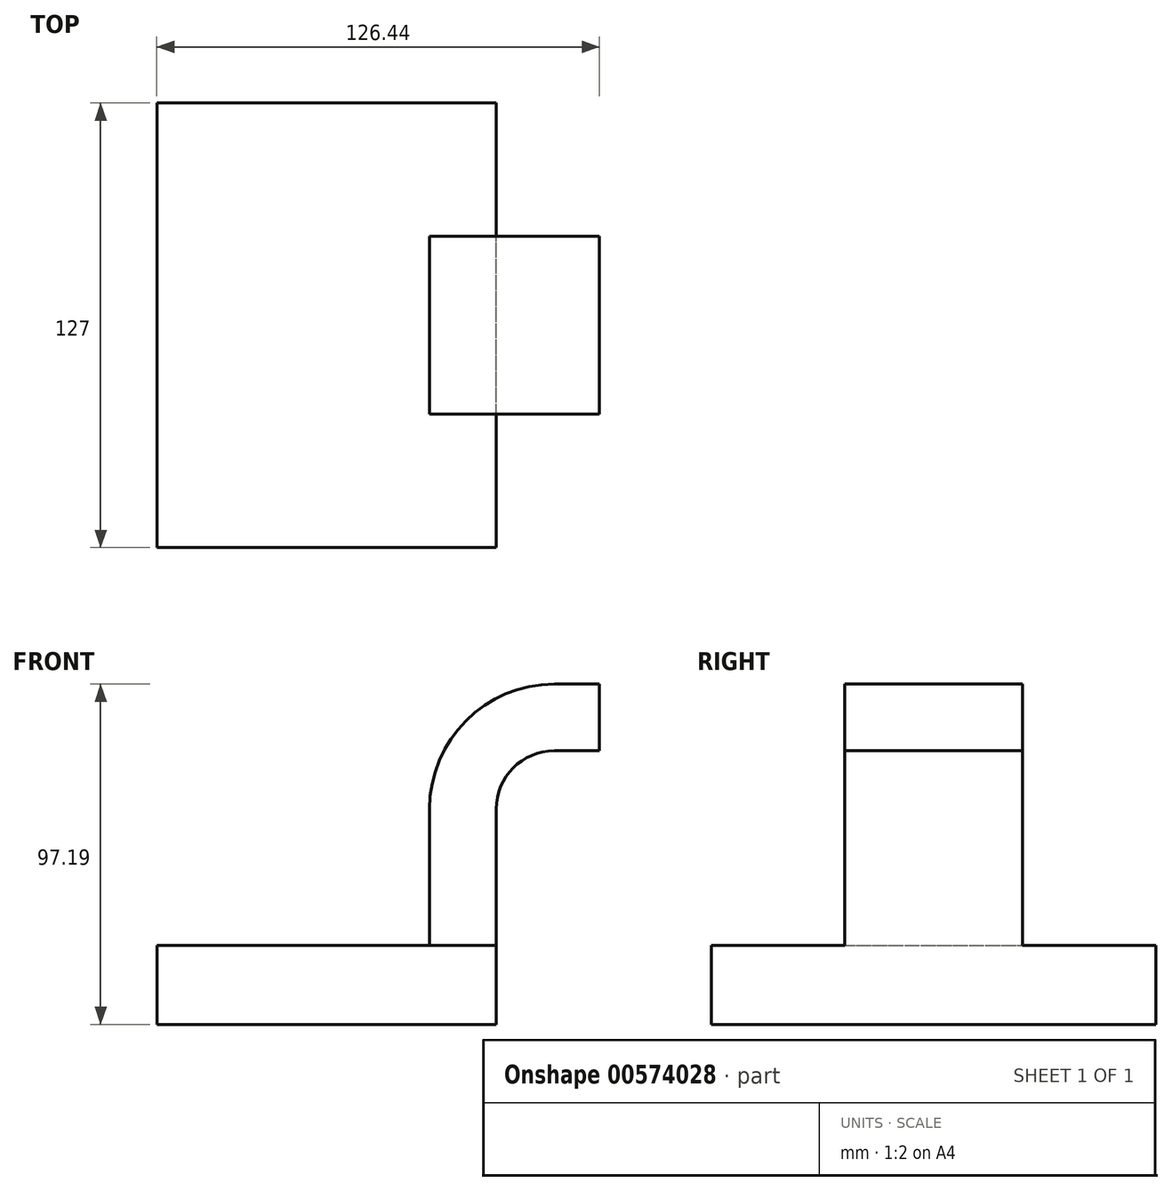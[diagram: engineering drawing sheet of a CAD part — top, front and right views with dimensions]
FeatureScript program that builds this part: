
annotation { "Feature Type Name" : "Feature", "Feature Type Description" : "" }
export const myFeature = defineFeature(function(context is Context, id is Id, definition is map)
    precondition{}
    {
        {
            var Q0;
            Q0=qCreatedBy(makeId("Front.planeOp"),FACE);
            var sketch = newSketch(context, id + "F0", { "sketchPlane" : qUnion([Q0])});
            skLineSegment(sketch, "E0.bottom", {"start": v(48.48, -11.3) * mm, "end": v(-48.48, -11.3) * mm});
            skLineSegment(sketch, "E0.top", {"start": v(48.48, 11.3) * mm, "end": v(-48.48, 11.3) * mm});
            skLineSegment(sketch, "E0.left", {"start": v(48.48, -11.3) * mm, "end": v(48.48, 11.3) * mm});
            skLineSegment(sketch, "E0.right", {"start": v(-48.48, -11.3) * mm, "end": v(-48.48, 11.3) * mm});
            skPoint(sketch, "E0.middle", {"position": v(0, 0) * mm});
            skLineSegment(sketch, "E1.bottom", {"start": v(135.43, 21.72) * mm, "end": v(77.96, 21.72) * mm});
            skLineSegment(sketch, "E1.top", {"start": v(135.43, 90.3) * mm, "end": v(77.96, 90.3) * mm});
            skLineSegment(sketch, "E1.left", {"start": v(135.43, 21.72) * mm, "end": v(135.43, 90.3) * mm});
            skLineSegment(sketch, "E1.right", {"start": v(77.96, 21.72) * mm, "end": v(77.96, 90.3) * mm});
            skPoint(sketch, "E1.middle", {"position": v(106.7, 56) * mm});
            skLineSegment(sketch, "E2", {"start": v(48.48, 11.3) * mm, "end": v(48.48, 50.22) * mm});
            skArc(sketch, "E3", {"start": v(48.48, 50.22) * mm, "mid": v(53.34, 61.97) * mm, "end": v(65.09, 66.84) * mm});
            skLineSegment(sketch, "E4", {"start": v(65.09, 66.84) * mm, "end": v(135.43, 66.84) * mm});
            skLineSegment(sketch, "E5.0", {"start": v(65.09, 85.89) * mm, "end": v(91.95, 85.89) * mm});
            skArc(sketch, "E5.1", {"start": v(29.43, 50.22) * mm, "mid": v(39.87, 75.44) * mm, "end": v(65.09, 85.89) * mm});
            skLineSegment(sketch, "E5.2", {"start": v(29.43, 7.75) * mm, "end": v(29.43, 50.22) * mm});
            skFitSpline(sketch, "E6", {"points": [v(-48.48, 11.3) * mm, v(65.09, 85.89) * mm], "startDerivative": vector(35.98, 132.5) * mm, "endDerivative": vector(154.78, -0.2) * mm});
            skSolve(sketch);
        }
        {
            var Q0;
            Q0=makeQuery(id+"F0.imprint","IMPRINT",FACE,{"disambiguationData":[TD([[makeQuery(id+"F0.imprint","IMPRINT",EDGE,{"derivedFrom":sQuery(id+"F0.wireOp",EDGE,"E0.bottom")}),-1.0]])]});
            extrude(context, id + "F1", {"entities" : qUnion([Q0]), "endBound" : BoundingType.SYMMETRIC, "depth" : 127 * mm, "offsetDistance" : 25.4 * mm});
        }
        {
            var Q0;
            {var subQ1=sQuery(id+"F0.wireOp",EDGE,"E2");Q0=makeQuery(id+"F0.imprint","IMPRINT",FACE,{"disambiguationData":[TD([[makeQuery(id+"F0.imprint","IMPRINT",EDGE,{"derivedFrom":subQ1}),1.0]])]});}
            extrude(context, id + "F2", {"entities" : qUnion([Q0]), "operationType" : NewBodyOperationType.ADD, "endBound" : BoundingType.SYMMETRIC, "depth" : 50.8 * mm, "offsetDistance" : 25.4 * mm});
        }
        {
            var Q0;
            {var subQ4=sQuery(id+"F0.wireOp",EDGE,"E5.1");Q0=makeQuery(id+"F0.imprint","IMPRINT",FACE,{"disambiguationData":[TD([[makeQuery(id+"F0.imprint","IMPRINT",EDGE,{"derivedFrom":subQ4}),1.0]])]});}
            extrude(context, id + "F3", {"entities" : qUnion([Q0]), "operationType" : NewBodyOperationType.ADD, "endBound" : BoundingType.SYMMETRIC, "depth" : 6.35 * mm, "offsetDistance" : 25.4 * mm});
        }
    });
